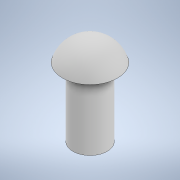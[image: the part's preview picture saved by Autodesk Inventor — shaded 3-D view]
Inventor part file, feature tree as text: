
AUTODESK INVENTOR PART (.ipt)
format: ipt  version: 2020 (Build 240168000, 168)  size: 117,760 bytes
history: native  units: in
note: dims shown in document units (in); Inventor stores cm internally (conversion verified against a paired STEP export)
features: revolve x1, sketch x1
ambient origin geometry x8: Origin, YZ Plane, XZ Plane, XY Plane, X Axis, Y Axis, Z Axis, Center Point
bodies: Solid1 (feature_tree)
feature tree (2):
  revolve  "Revolution1"  [1 undecoded]
  sketch  "Sketch1"  dims[d0=0.65in d1=0.125in d2=0.5in d3=0.075in d4=0.208in d5=90.0deg]
note: 1 required parameter value undecoded (feature->parameter linkage not recoverable at this tier; creation-order binding heuristic only, values carry confidence <= 0.55)
